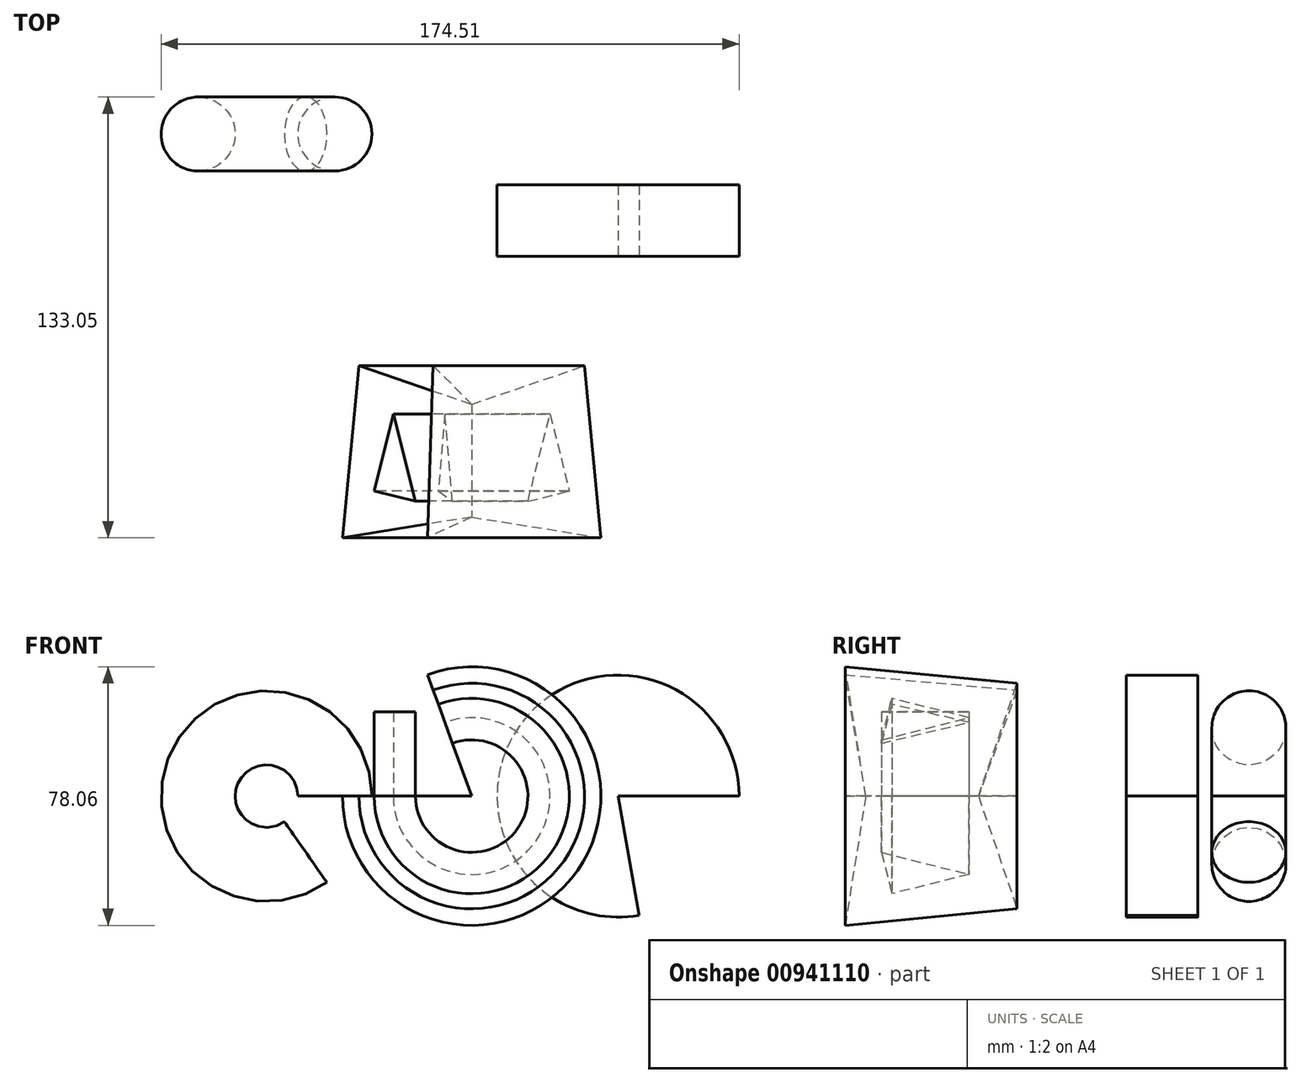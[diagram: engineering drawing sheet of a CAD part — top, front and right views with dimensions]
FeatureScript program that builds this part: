
annotation { "Feature Type Name" : "Feature", "Feature Type Description" : "" }
export const myFeature = defineFeature(function(context is Context, id is Id, definition is map)
    precondition{}
    {
        {
            var Q0;
            Q0=qCreatedBy(makeId("Top.planeOp"),FACE);
            var sketch = newSketch(context, id + "F0", { "sketchPlane" : qUnion([Q0])});
            skCircle(sketch, "E0", {"center": v(-62.28, 52.52) * mm, "radius": 11.18 * mm});
            skLineSegment(sketch, "E1.bottom", {"start": v(23.25, 37.16) * mm, "end": v(59.79, 37.16) * mm});
            skLineSegment(sketch, "E1.top", {"start": v(23.25, 15.57) * mm, "end": v(59.79, 15.57) * mm});
            skLineSegment(sketch, "E1.left", {"start": v(23.25, 37.16) * mm, "end": v(23.25, 15.57) * mm});
            skLineSegment(sketch, "E1.right", {"start": v(59.79, 37.16) * mm, "end": v(59.79, 15.57) * mm});
            skLineSegment(sketch, "E2", {"start": v(-55, -17.45) * mm, "end": v(-20.95, -29.08) * mm});
            skLineSegment(sketch, "E3", {"start": v(-20.95, -29.08) * mm, "end": v(-20.95, -63.13) * mm});
            skLineSegment(sketch, "E4", {"start": v(-20.95, -63.13) * mm, "end": v(-59.98, -69.35) * mm});
            skLineSegment(sketch, "E5", {"start": v(-59.98, -69.35) * mm, "end": v(-55, -17.45) * mm});
            skLineSegment(sketch, "E6", {"start": v(-44.62, -31.99) * mm, "end": v(-50.43, -55.24) * mm});
            skLineSegment(sketch, "E7", {"start": v(-50.43, -55.24) * mm, "end": v(-37.93, -58.36) * mm});
            skLineSegment(sketch, "E8", {"start": v(-37.93, -58.36) * mm, "end": v(-44.62, -31.99) * mm});
            skLineSegment(sketch, "E9", {"start": v(-82.91, 71.7) * mm, "end": v(-82.91, 30.26) * mm, "construction": true});
            skSolve(sketch);
        }
        {
            var Q0;
            Q0=makeQuery(id+"F0.imprint","IMPRINT",FACE,{"disambiguationData":[TD([[makeQuery(id+"F0.imprint","IMPRINT",EDGE,{"derivedFrom":sQuery(id+"F0.wireOp",EDGE,"E1.bottom")}),-1.0]])]});
            var Q1;
            Q1=sQuery(id+"F0.wireOp",EDGE,"E1.left");
            revolve(context, id + "F1", {"surfaceOperationType" : NewSurfaceOperationType.NEW, "entities" : qUnion([Q0]), "axis" : qUnion([Q1]), "revolveType" : RevolveType.ONE_DIRECTION, "angle" : 280 * degree});
        }
        {
            var Q0;
            Q0=makeQuery(id+"F0.imprint","IMPRINT",FACE,{"disambiguationData":[TD([[makeQuery(id+"F0.imprint","IMPRINT",EDGE,{"derivedFrom":sQuery(id+"F0.wireOp",EDGE,"E0")}),1.0]])]});
            var Q1;
            Q1=sQuery(id+"F0.wireOp",EDGE,"E9");
            revolve(context, id + "F2", {"surfaceOperationType" : NewSurfaceOperationType.NEW, "entities" : qUnion([Q0]), "axis" : qUnion([Q1]), "revolveType" : RevolveType.ONE_DIRECTION, "angle" : 305 * degree});
        }
        {
            var Q0;
            Q0=makeQuery(id+"F0.imprint","IMPRINT",FACE,{"disambiguationData":[TD([[makeQuery(id+"F0.imprint","IMPRINT",EDGE,{"derivedFrom":sQuery(id+"F0.wireOp",EDGE,"E6")}),1.0]])]});
            extrude(context, id + "F3", {"entities" : qUnion([Q0]), "depth" : 25.4 * mm, "offsetDistance" : 25.4 * mm});
        }
        {
            var Q0;
            Q0=makeQuery(id+"F0.imprint","IMPRINT",FACE,{"disambiguationData":[TD([[makeQuery(id+"F0.imprint","IMPRINT",EDGE,{"derivedFrom":sQuery(id+"F0.wireOp",EDGE,"E2")}),-1.0]])]});
            var Q1;
            Q1=sQuery(id+"F0.wireOp",EDGE,"E3");
            revolve(context, id + "F4", {"surfaceOperationType" : NewSurfaceOperationType.NEW, "entities" : qUnion([Q0]), "axis" : qUnion([Q1]), "revolveType" : RevolveType.ONE_DIRECTION, "angle" : 290 * degree});
        }
    });
